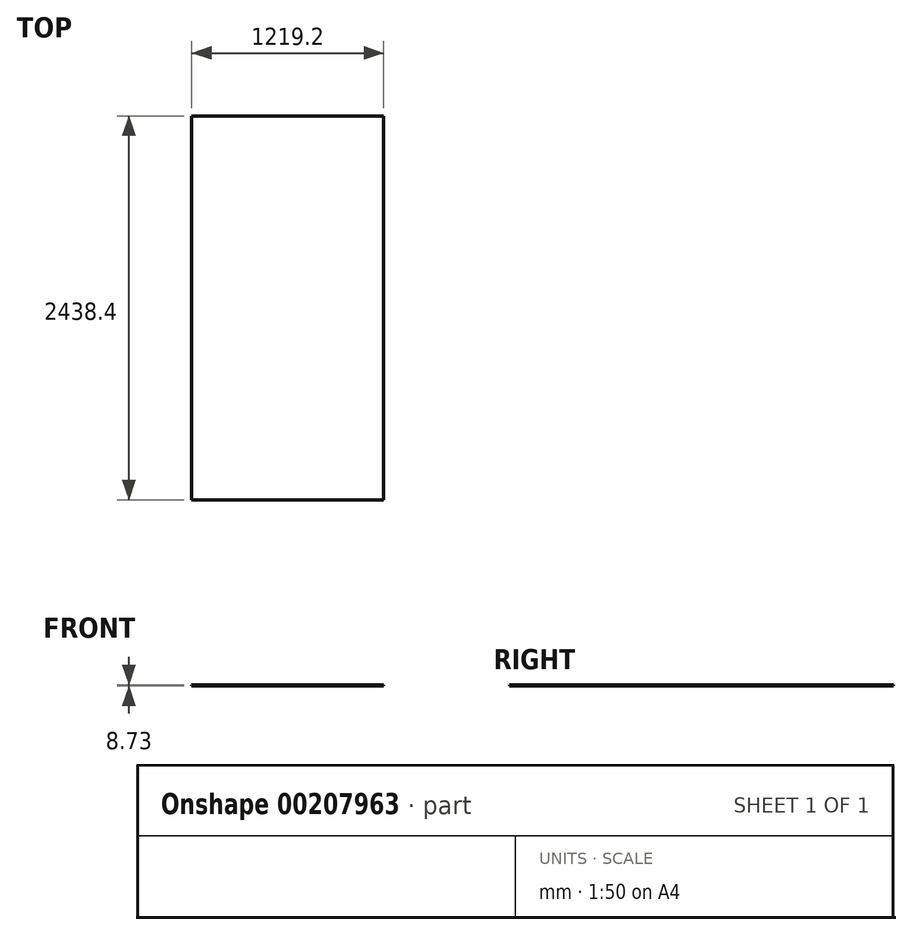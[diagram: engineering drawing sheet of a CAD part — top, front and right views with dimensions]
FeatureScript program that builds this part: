
annotation { "Feature Type Name" : "Feature", "Feature Type Description" : "" }
export const myFeature = defineFeature(function(context is Context, id is Id, definition is map)
    precondition{}
    {
        {
            var Q0;
            Q0=qCreatedBy(makeId("Top.planeOp"),FACE);
            var sketch = newSketch(context, id + "F0", { "sketchPlane" : qUnion([Q0])});
            skLineSegment(sketch, "E0.bottom", {"start": v(0, 0) * mm, "end": v(1219.2, 0) * mm});
            skLineSegment(sketch, "E0.top", {"start": v(0, -2438.4) * mm, "end": v(1219.2, -2438.4) * mm});
            skLineSegment(sketch, "E0.left", {"start": v(0, 0) * mm, "end": v(0, -2438.4) * mm});
            skLineSegment(sketch, "E0.right", {"start": v(1219.2, 0) * mm, "end": v(1219.2, -2438.4) * mm});
            skSolve(sketch);
        }
        {
            var Q0;
            Q0 = qSketchRegion(id + "F0", true);
            extrude(context, id + "F1", {"entities" : qUnion([Q0]), "depth" : 8.73 * mm});
        }
    });
